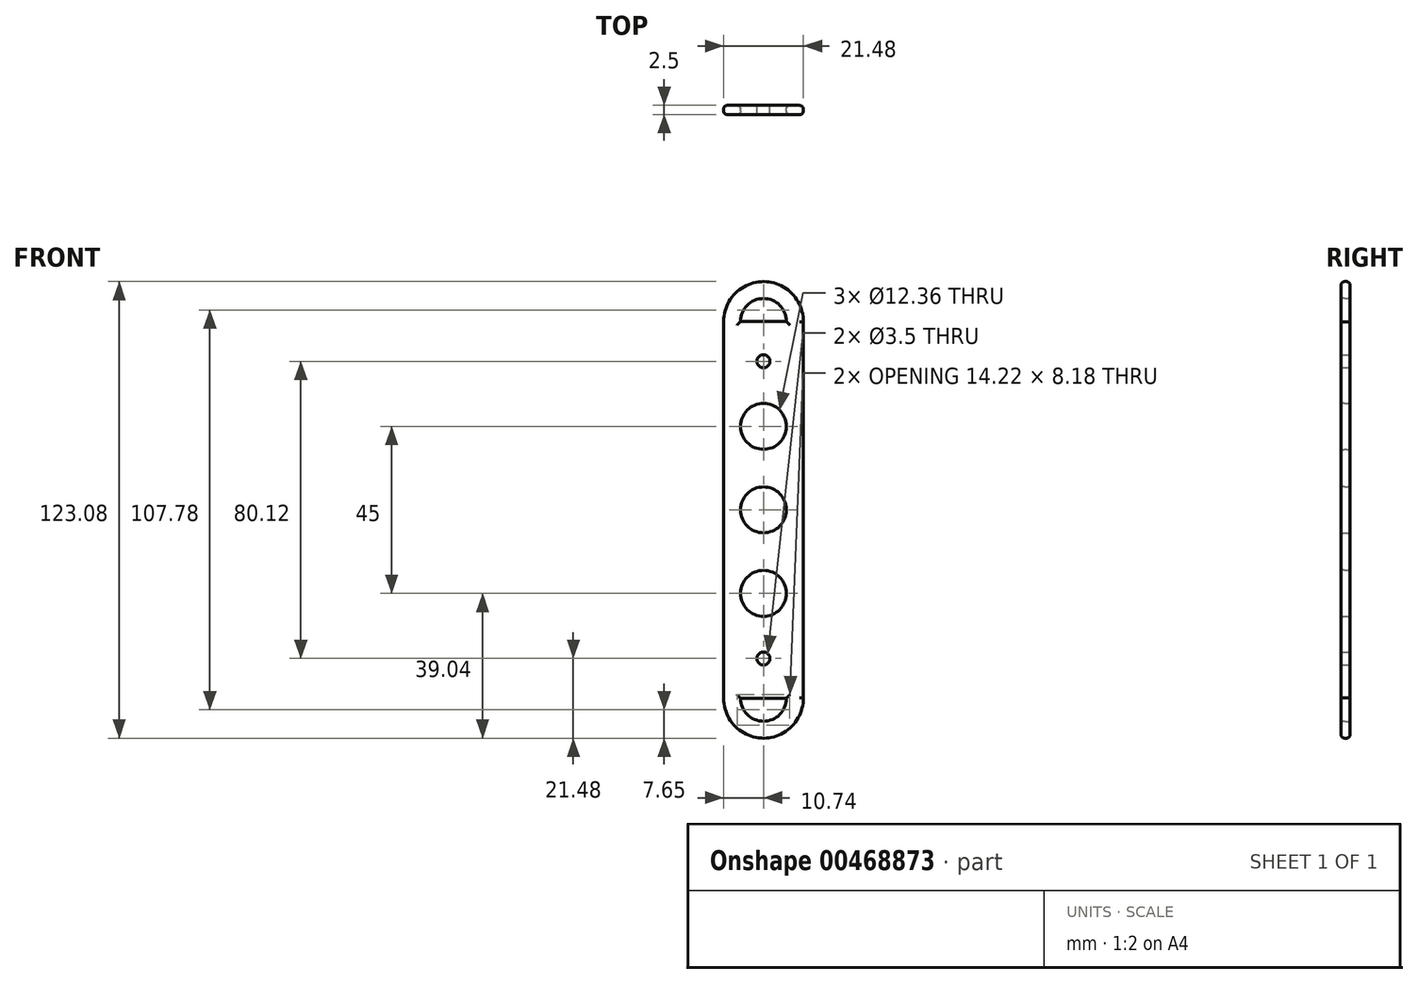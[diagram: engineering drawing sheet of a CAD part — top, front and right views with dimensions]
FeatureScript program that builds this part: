
annotation { "Feature Type Name" : "Feature", "Feature Type Description" : "" }
export const myFeature = defineFeature(function(context is Context, id is Id, definition is map)
    precondition{}
    {
        {
            var Q0;
            Q0=qCreatedBy(makeId("Front.planeOp"),FACE);
            var sketch = newSketch(context, id + "F0", { "sketchPlane" : qUnion([Q0])});
            skPoint(sketch, "E0.middle", {"position": v(0, 0) * mm});
            skLineSegment(sketch, "E1", {"start": v(0, -25.61) * mm, "end": v(0, -29.11) * mm});
            skLineSegment(sketch, "E2", {"start": v(0, 51) * mm, "end": v(0, 54.51) * mm});
            skArc(sketch, "E3", {"start": v(-6.18, -38.1) * mm, "mid": v(0, -44.28) * mm, "end": v(6.18, -38.1) * mm});
            skArc(sketch, "E4", {"start": v(-10.74, -38.1) * mm, "mid": v(0.07, -48.84) * mm, "end": v(10.74, -37.97) * mm});
            skCircle(sketch, "E5", {"center": v(0, -27.36) * mm, "radius": 1.75 * mm});
            skLineSegment(sketch, "E6", {"start": v(6.18, -38.1) * mm, "end": v(-6.18, -38.1) * mm});
            skLineSegment(sketch, "E7", {"start": v(-6.18, -38.1) * mm, "end": v(-6.18, -38.1) * mm});
            skArc(sketch, "E8", {"start": v(6.18, 63.5) * mm, "mid": v(0, 69.68) * mm, "end": v(-6.18, 63.5) * mm});
            skArc(sketch, "E9", {"start": v(10.74, 63.37) * mm, "mid": v(0.07, 74.24) * mm, "end": v(-10.74, 63.5) * mm});
            skCircle(sketch, "E10", {"center": v(0, 52.76) * mm, "radius": 1.75 * mm});
            skLineSegment(sketch, "E11", {"start": v(6.18, 63.5) * mm, "end": v(-6.18, 63.5) * mm});
            skLineSegment(sketch, "E12", {"start": v(-10.74, 63.5) * mm, "end": v(-10.74, -38.1) * mm});
            skLineSegment(sketch, "E13", {"start": v(10.74, -37.97) * mm, "end": v(10.74, 63.63) * mm});
            skLineSegment(sketch, "E14", {"start": v(6.18, 12.7) * mm, "end": v(-6.18, 12.7) * mm, "construction": true});
            skCircle(sketch, "E15", {"center": v(0, 12.7) * mm, "radius": 6.18 * mm});
            skCircle(sketch, "E16.0.1.0", {"center": v(0, 35.2) * mm, "radius": 6.18 * mm});
            skLineSegment(sketch, "E16.direction1", {"start": v(0, 12.7) * mm, "end": v(25, 12.7) * mm, "construction": true});
            skLineSegment(sketch, "E16.direction2", {"start": v(0, 12.7) * mm, "end": v(0, 35.2) * mm, "construction": true});
            skCircle(sketch, "E17.0.1.0", {"center": v(0, -9.8) * mm, "radius": 6.18 * mm});
            skLineSegment(sketch, "E17.direction2", {"start": v(0, 12.7) * mm, "end": v(0, -9.8) * mm, "construction": true});
            skSolve(sketch);
        }
        {
            var Q0;
            Q0=qSketchRegion(id+"F0",true);
            extrude(context, id + "F1", {"entities" : qUnion([Q0]), "depth" : 2.5 * mm});
        }
        {
            var Q0;
            Q0=makeQuery(id+"F1.opExtrude","CAP_EDGE",EDGE,{"disambiguationData":[OSD([sQuery(id+"F0.wireOp",EDGE,"E8")])],"isStart":false});
            var Q1;
            Q1=makeQuery(id+"F1.opExtrude","CAP_EDGE",EDGE,{"disambiguationData":[OSD([sQuery(id+"F0.wireOp",EDGE,"E8")])],"isStart":true});
            var Q2;
            Q2=makeQuery(id+"F1.opExtrude","CAP_EDGE",EDGE,{"disambiguationData":[OSD([sQuery(id+"F0.wireOp",EDGE,"E11")])],"isStart":false});
            var Q3;
            Q3=makeQuery(id+"F1.opExtrude","CAP_EDGE",EDGE,{"disambiguationData":[OSD([sQuery(id+"F0.wireOp",EDGE,"E11")])],"isStart":true});
            var Q4;
            Q4=makeQuery(id+"F1.opExtrude","CAP_EDGE",EDGE,{"disambiguationData":[OSD([sQuery(id+"F0.wireOp",EDGE,"E9")])],"isStart":false});
            var Q5;
            Q5=makeQuery(id+"F1.opExtrude","CAP_EDGE",EDGE,{"disambiguationData":[OSD([sQuery(id+"F0.wireOp",EDGE,"E9")])],"isStart":true});
            var Q6;
            Q6=makeQuery(id+"F1.opExtrude","CAP_EDGE",EDGE,{"disambiguationData":[OSD([sQuery(id+"F0.wireOp",EDGE,"E16.0.1.0")])],"isStart":false});
            var Q7;
            Q7=makeQuery(id+"F1.opExtrude","CAP_EDGE",EDGE,{"disambiguationData":[OSD([sQuery(id+"F0.wireOp",EDGE,"E16.0.1.0")])],"isStart":true});
            var Q8;
            Q8=makeQuery(id+"F1.opExtrude","CAP_EDGE",EDGE,{"disambiguationData":[OSD([sQuery(id+"F0.wireOp",EDGE,"E15")])],"isStart":false});
            var Q9;
            Q9=makeQuery(id+"F1.opExtrude","CAP_EDGE",EDGE,{"disambiguationData":[OSD([sQuery(id+"F0.wireOp",EDGE,"E15")])],"isStart":true});
            var Q10;
            Q10=makeQuery(id+"F1.opExtrude","CAP_EDGE",EDGE,{"disambiguationData":[OSD([sQuery(id+"F0.wireOp",EDGE,"E17.0.1.0")])],"isStart":false});
            var Q11;
            Q11=makeQuery(id+"F1.opExtrude","CAP_EDGE",EDGE,{"disambiguationData":[OSD([sQuery(id+"F0.wireOp",EDGE,"E17.0.1.0")])],"isStart":true});
            var Q12;
            Q12=makeQuery(id+"F1.opExtrude","CAP_EDGE",EDGE,{"disambiguationData":[OSD([sQuery(id+"F0.wireOp",EDGE,"E6")])],"isStart":false});
            var Q13;
            Q13=makeQuery(id+"F1.opExtrude","CAP_EDGE",EDGE,{"disambiguationData":[OSD([sQuery(id+"F0.wireOp",EDGE,"E6")])],"isStart":true});
            var Q14;
            Q14=makeQuery(id+"F1.opExtrude","CAP_EDGE",EDGE,{"disambiguationData":[OSD([sQuery(id+"F0.wireOp",EDGE,"E3")])],"isStart":true});
            var Q15;
            Q15=makeQuery(id+"F1.opExtrude","CAP_EDGE",EDGE,{"disambiguationData":[OSD([sQuery(id+"F0.wireOp",EDGE,"E3")])],"isStart":false});
            fillet(context, id + "F2", {"entities" : qUnion([Q0, Q1, Q2, Q3, Q4, Q5, Q6, Q7, Q8, Q9, Q10, Q11, Q12, Q13, Q14, Q15]), "radius" : 1 * mm, "tangentPropagation" : true, "allowEdgeOverflow" : false});
        }
    });
